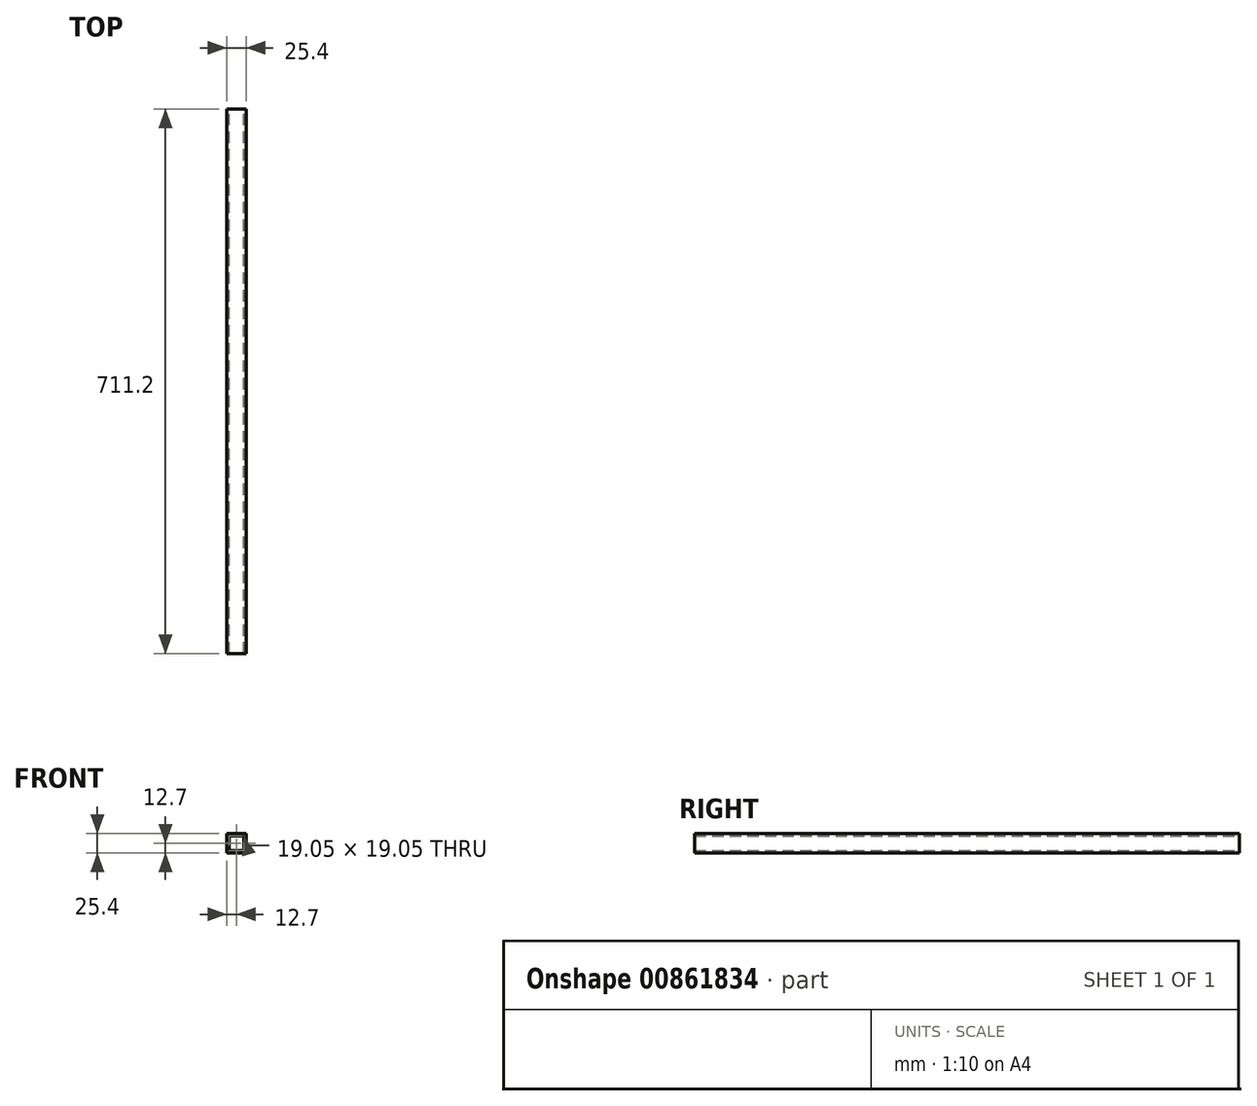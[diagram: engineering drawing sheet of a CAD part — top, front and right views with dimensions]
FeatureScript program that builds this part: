
annotation { "Feature Type Name" : "Feature", "Feature Type Description" : "" }
export const myFeature = defineFeature(function(context is Context, id is Id, definition is map)
    precondition{}
    {
        {
            var Q0;
            Q0=qCreatedBy(makeId("Front.planeOp"),FACE);
            var sketch = newSketch(context, id + "F0", { "sketchPlane" : qUnion([Q0])});
            skLineSegment(sketch, "E0.bottom", {"start": v(12.7, 12.7) * mm, "end": v(-12.7, 12.7) * mm});
            skLineSegment(sketch, "E0.top", {"start": v(12.7, -12.7) * mm, "end": v(-12.7, -12.7) * mm});
            skLineSegment(sketch, "E0.left", {"start": v(12.7, 12.7) * mm, "end": v(12.7, -12.7) * mm});
            skLineSegment(sketch, "E0.right", {"start": v(-12.7, 12.7) * mm, "end": v(-12.7, -12.7) * mm});
            skPoint(sketch, "E0.middle", {"position": v(0, 0) * mm});
            skLineSegment(sketch, "E1.bottom", {"start": v(9.53, 9.53) * mm, "end": v(-9.52, 9.53) * mm});
            skLineSegment(sketch, "E1.top", {"start": v(9.52, -9.53) * mm, "end": v(-9.53, -9.53) * mm});
            skLineSegment(sketch, "E1.left", {"start": v(9.53, 9.53) * mm, "end": v(9.53, -9.53) * mm});
            skLineSegment(sketch, "E1.right", {"start": v(-9.53, 9.53) * mm, "end": v(-9.53, -9.53) * mm});
            skSolve(sketch);
        }
        {
            var Q0;
            Q0=makeQuery(id+"F0.imprint","IMPRINT",FACE,{"disambiguationData":[TD([[makeQuery(id+"F0.imprint","IMPRINT",EDGE,{"derivedFrom":sQuery(id+"F0.wireOp",EDGE,"E0.bottom")}),1.0]])]});
            extrude(context, id + "F1", {"entities" : qUnion([Q0]), "depth" : 711.2 * mm, "offsetDistance" : 25.4 * mm, "symmetric" : true});
        }
    });
